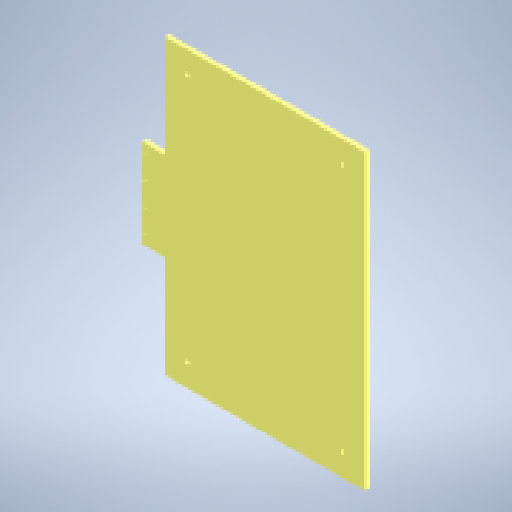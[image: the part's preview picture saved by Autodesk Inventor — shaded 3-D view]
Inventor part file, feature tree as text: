
AUTODESK INVENTOR PART (.ipt)
format: ipt  version: 2024 (Build 280153000, 153)  size: 315,904 bytes
history: native  units: mm
features: extrude x2, sketch x2
ambient origin geometry x8: Origin, YZ Plane, XZ Plane, XY Plane, X Axis, Y Axis, Z Axis, Center Point
bodies: Solido1 (feature_tree)
feature tree (4):
  extrude  "Estrusione1"  Depth=450.0mm
  extrude  "Estrusione2"  Depth=660.0mm
  sketch  "Schizzo1"
  sketch  "Schizzo2"
